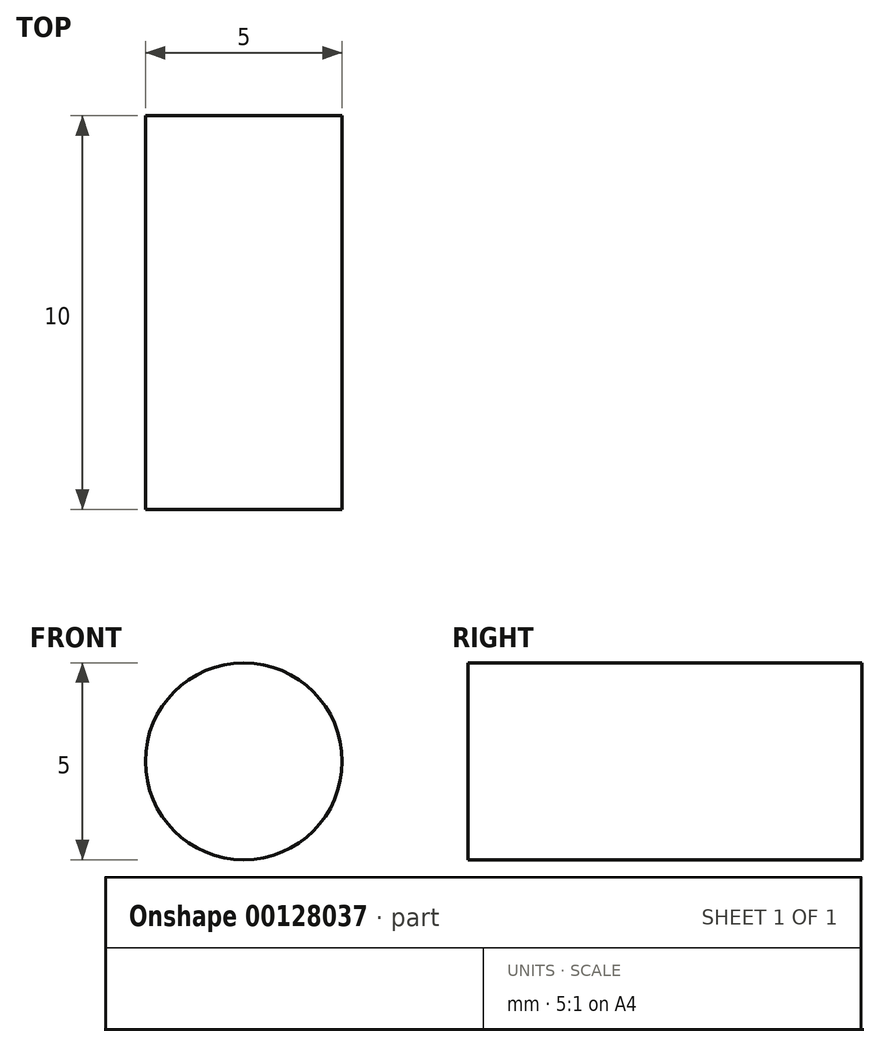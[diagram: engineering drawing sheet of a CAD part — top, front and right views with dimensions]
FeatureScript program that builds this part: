
annotation { "Feature Type Name" : "Feature", "Feature Type Description" : "" }
export const myFeature = defineFeature(function(context is Context, id is Id, definition is map)
    precondition{}
    {
        {
            var Q0;
            Q0=qCreatedBy(makeId("Front.planeOp"),FACE);
            var sketch = newSketch(context, id + "F0", { "sketchPlane" : qUnion([Q0])});
            skCircle(sketch, "E0", {"center": v(0, 0) * mm, "radius": 2.5 * mm});
            skSolve(sketch);
        }
        {
            var Q0;
            Q0 = qSketchRegion(id + "F0", true);
            extrude(context, id + "F1", {"entities" : qUnion([Q0]), "depth" : 10 * mm});
        }
    });
